# Revit family: Gira_547300
name_source: partatom
category: Electrical Fixtures
revit_build: Autodesk Revit 2017 (Build: 20160225_1515(x64)
units: mm (PartAtom-declared; Revit-internal decimal feet)

## family parameters
Cut with Voids When Loaded = No
Host = Face
Maintain Annotation Orientation = No
Part Type = Normal
Room Calculation Point = No
Round Connector Dimension = Use Diameter
Shared = No

## types (1)
- WL energy sens. 4-g DRA Gira eNet
    Anschlussart = Direct
    BIM = https://media.live.bim.site 8f.rfa
    BIMSITE_PRODUCT_ID = 996cdf7b99e2f293fb83e3a053500779b17a33f8
    Blindleistung = No
    Bus connection included = No
    Cost = 0 $
    Default Elevation = 1219 mm
    Description = WL energy sens.4g DRA eNet eNet wireless energy sensor, 4-gang,DRA Features: - The eNet wireless energy sensors enable the wireless transmission of voltage, electricity, and energy values to the eNet server. - Operation with an eNet server. - Logging electricity and voltage of the connected device. - Calculation of effective output, reactive power, apparent power, and active electrical energy. - Event-controlled or time-controlled transmission of measurement value telegrams to the eNet server. - Time synchronisation with the eNet server. - Display of energy values possible via the eNet SMART HOME app. - Use of energy values as a trigger for IF THEN rules in the eNet Smart Home app. Can be set with eNet server:: - Localisation of the device. - Fully encrypted wireless transmission (AES CCM) from eNet Server software version 2.0. - Use power consumption as the 'IF' condition in IF THEN rules to activate actions, scenes, and timers. - Device software update.,Notes : - An eNet server is required to operate this DIN-rail mounting device.
    GTIN = 4010337774372
    HAN = 547300
    Handschaltung = No
    HeinzeBIM = https://www.heinze.de
    LED controlling = No
    Local operation/hand operation = No
    Manufacturer = Gira
    Max. number of venetian-blind outputs = 0
    Max. switching current [Ampere] = 0
    Max. switching power [Voltampere] = 0
    Model = Energy meter
    Modulare Erweiterungsmöglichkeit = No
    Number of binary inputs = 0
    Number of inputs = 0
    Number of outputs = 0
    Rated current [Ampere] = 0
    S0 Impulsschnittstelle = ohne (*de-DE)
    Stellgröße schaltend = No
    Stellgröße stetig = No
    Suitable for C-load = No
    Switching current (resistive) [Ampere] = 0
    Tarifumschaltung = No
    URL = https://www.gira.de
    Ventilschutzfunktion = No
    Verschiedene Phasen anschließbar = No
    With switch function = No
    Zulassung nach PTB = No

## geometry (parser evidence)
native form markers: Blend x2, Sweep x3
no freeform markers — native parametric forms only
